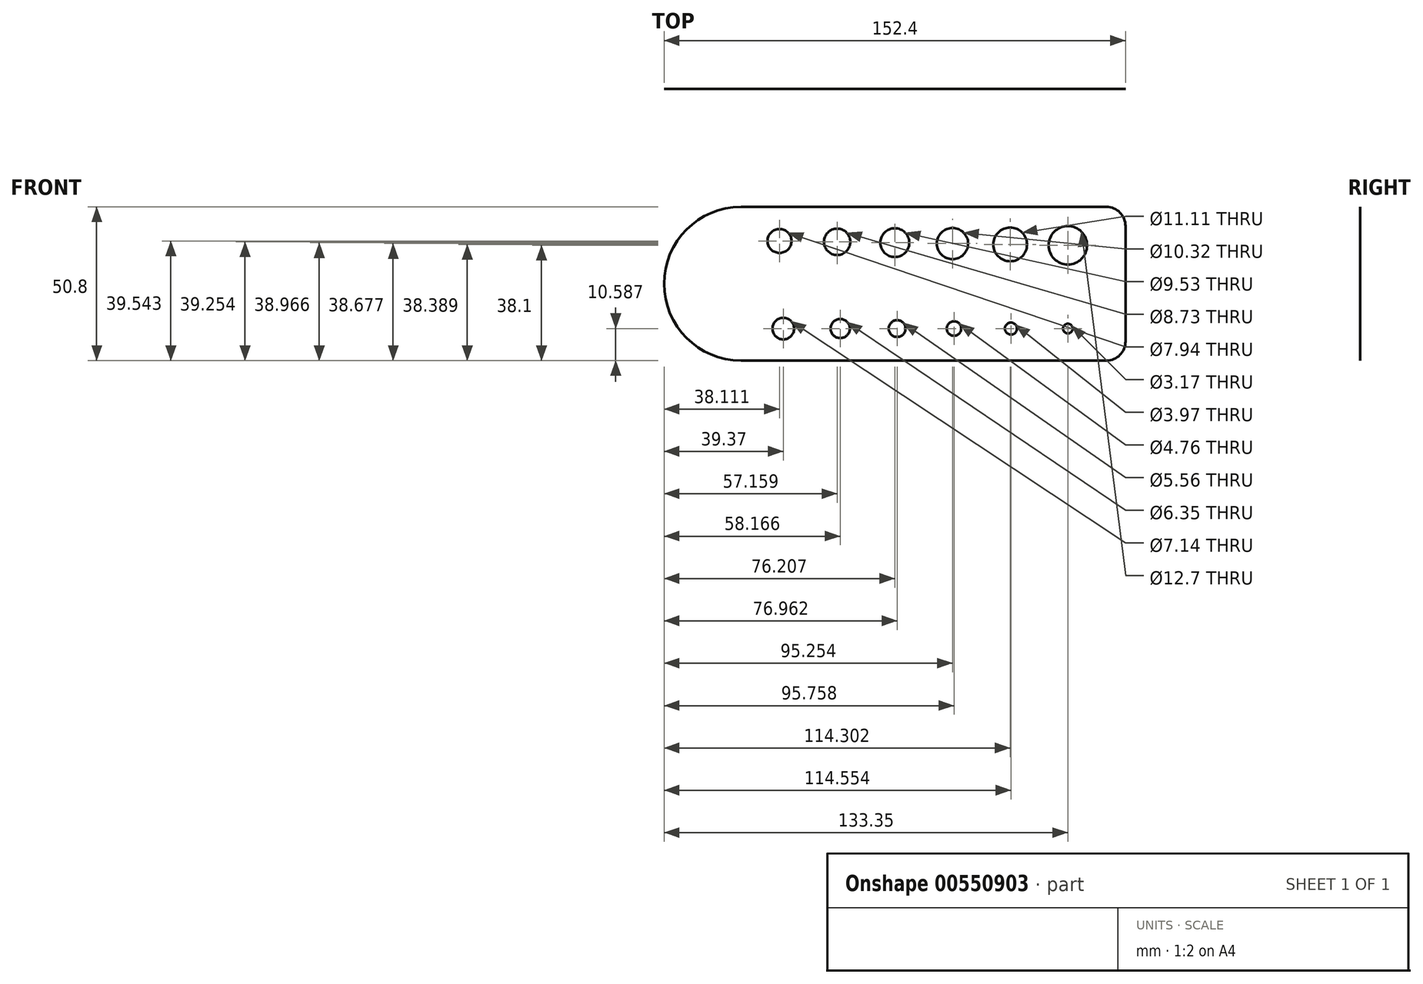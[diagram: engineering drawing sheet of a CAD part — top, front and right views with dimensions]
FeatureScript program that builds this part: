
annotation { "Feature Type Name" : "Feature", "Feature Type Description" : "" }
export const myFeature = defineFeature(function(context is Context, id is Id, definition is map)
    precondition{}
    {
        {
            var Q0;
            Q0=qCreatedBy(makeId("Front.planeOp"),FACE);
            var sketch = newSketch(context, id + "F0", { "sketchPlane" : qUnion([Q0])});
            skLineSegment(sketch, "E0.bottom", {"start": v(0, 0) * mm, "end": v(120.65, 0) * mm});
            skLineSegment(sketch, "E0.top", {"start": v(0, 50.8) * mm, "end": v(120.65, 50.8) * mm});
            skLineSegment(sketch, "E0.left", {"start": v(0, 0) * mm, "end": v(0, 50.8) * mm});
            skLineSegment(sketch, "E0.right", {"start": v(127, 6.35) * mm, "end": v(127, 44.45) * mm});
            skPoint(sketch, "E1.visualSharp", {"position": v(127, 50.8) * mm});
            skArc(sketch, "E1.filletArc", {"start": v(127, 44.45) * mm, "mid": v(125.14, 48.94) * mm, "end": v(120.65, 50.8) * mm});
            skPoint(sketch, "E2.visualSharp", {"position": v(127, 0) * mm});
            skArc(sketch, "E2.filletArc", {"start": v(120.65, 0) * mm, "mid": v(125.14, 1.86) * mm, "end": v(127, 6.35) * mm});
            skArc(sketch, "E3", {"start": v(0, 50.8) * mm, "mid": v(-25.4, 25.4) * mm, "end": v(0, 0) * mm});
            skPoint(sketch, "E4.orphan", {"position": v(25.4, 25.4) * mm});
            skPoint(sketch, "E5.orphan", {"position": v(25.4, 0) * mm});
            skPoint(sketch, "E6.start.orphan", {"position": v(25.4, 50.8) * mm});
            skCircle(sketch, "E7", {"center": v(107.95, 38.1) * mm, "radius": 6.35 * mm});
            skCircle(sketch, "E8.1.0.0", {"center": v(88.9, 38.39) * mm, "radius": 5.56 * mm});
            skCircle(sketch, "E8.2.0.0", {"center": v(69.85, 38.68) * mm, "radius": 5.16 * mm});
            skCircle(sketch, "E8.3.0.0", {"center": v(50.8, 38.97) * mm, "radius": 4.76 * mm});
            skCircle(sketch, "E8.4.0.0", {"center": v(31.76, 39.25) * mm, "radius": 4.37 * mm});
            skCircle(sketch, "E8.5.0.0", {"center": v(12.71, 39.54) * mm, "radius": 3.97 * mm});
            skLineSegment(sketch, "E8.direction1", {"start": v(107.95, 38.1) * mm, "end": v(88.9, 38.39) * mm, "construction": true});
            skCircle(sketch, "E9", {"center": v(107.95, 10.59) * mm, "radius": 1.59 * mm});
            skCircle(sketch, "E10.1.0.0", {"center": v(89.15, 10.59) * mm, "radius": 1.98 * mm});
            skCircle(sketch, "E10.2.0.0", {"center": v(70.36, 10.59) * mm, "radius": 2.38 * mm});
            skCircle(sketch, "E10.3.0.0", {"center": v(51.56, 10.59) * mm, "radius": 2.78 * mm});
            skCircle(sketch, "E10.4.0.0", {"center": v(32.77, 10.59) * mm, "radius": 3.18 * mm});
            skCircle(sketch, "E10.5.0.0", {"center": v(13.97, 10.59) * mm, "radius": 3.57 * mm});
            skLineSegment(sketch, "E10.direction1", {"start": v(107.95, 10.59) * mm, "end": v(89.15, 10.59) * mm, "construction": true});
            skSolve(sketch);
        }
        {
            var Q0;
            Q0 = qSketchRegion(id + "F0", true);
            extrude(context, id + "F1", {"entities" : qUnion([Q0]), "depth" : 1 / 203.2 * mm, "offsetDistance" : 25.4 * mm});
        }
    });
